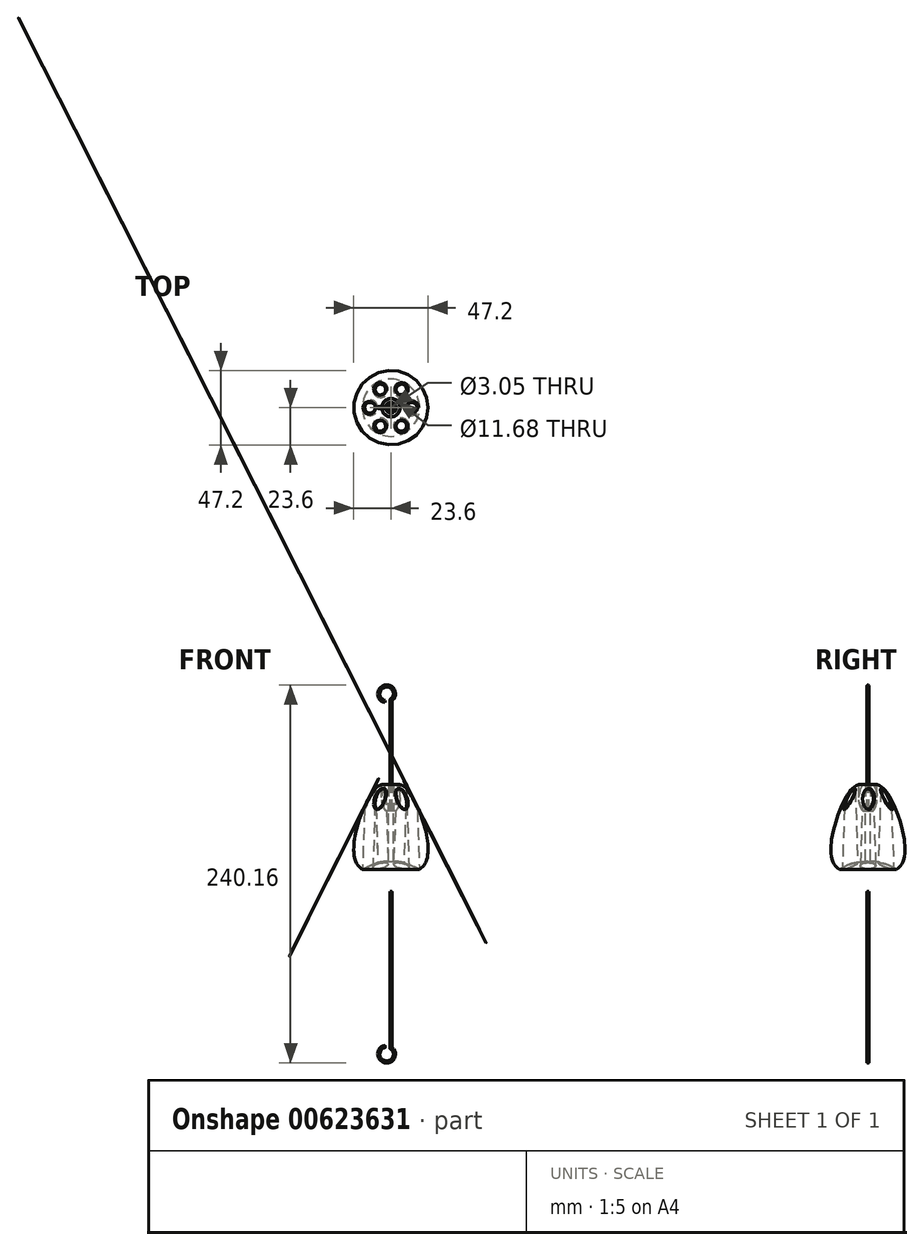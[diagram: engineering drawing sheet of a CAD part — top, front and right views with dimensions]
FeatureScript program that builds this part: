
annotation { "Feature Type Name" : "Feature", "Feature Type Description" : "" }
export const myFeature = defineFeature(function(context is Context, id is Id, definition is map)
    precondition{}
    {
        {
            var Q0;
            Q0=qCreatedBy(makeId("Front.planeOp"),FACE);
            var sketch = newSketch(context, id + "F0", { "sketchPlane" : qUnion([Q0])});
            skLineSegment(sketch, "E0", {"start": v(0, 64.62) * mm, "end": v(0, -10.1) * mm, "construction": true});
            skLineSegment(sketch, "E1", {"start": v(-12.7, 50.8) * mm, "end": v(12.7, 50.8) * mm, "construction": true});
            skLineSegment(sketch, "E2", {"start": v(-22.22, 7.62) * mm, "end": v(22.23, 7.62) * mm, "construction": true});
            skFitSpline(sketch, "E3", {"points": [v(0, 0) * mm, v(-22.23, 7.62) * mm, v(-12.7, 50.8) * mm, v(0, 57.15) * mm], "startDerivative": vector(-86.95, 0.17) * mm, "endDerivative": vector(69.55, -6.02) * mm});
            skLineSegment(sketch, "E4", {"start": v(-5.84, 48.51) * mm, "end": v(5.84, 48.51) * mm, "construction": true});
            skLineSegment(sketch, "E5", {"start": v(-3.3, 39.88) * mm, "end": v(0, 39.88) * mm});
            skArc(sketch, "E6", {"start": v(-5.84, 48.51) * mm, "mid": v(-5.2, 44.01) * mm, "end": v(-3.3, 39.88) * mm});
            skLineSegment(sketch, "E7", {"start": v(-5.84, 48.51) * mm, "end": v(-5.84, 56.75) * mm});
            skPoint(sketch, "E8.orphan", {"position": v(-3.3, 57.15) * mm});
            skPoint(sketch, "E9.orphan", {"position": v(3.3, 39.88) * mm});
            skPoint(sketch, "E10.end.orphan", {"position": v(3.3, 57.15) * mm});
            skLineSegment(sketch, "E11", {"start": v(0, 39.88) * mm, "end": v(0, 0) * mm});
            skSolve(sketch);
        }
        {
            var Q0;
            Q0 = qSketchRegion(id + "F0", true);
            var Q1;
            Q1=sQuery(id+"F0.wireOp",EDGE,"E0");
            revolve(context, id + "F1", {"entities" : qUnion([Q0]), "axis" : qUnion([Q1]), "revolveType" : RevolveType.FULL});
        }
        {
            var Q0;
            Q0=makeQuery(id+"F1.opRevolve","SWEPT_FACE",FACE,{"disambiguationData":[OSD([sQuery(id+"F0.wireOp",EDGE,"E5")])]});
            var sketch = newSketch(context, id + "F2", { "sketchPlane" : qUnion([Q0])});
            skCircle(sketch, "E12", {"center": v(0, 0) * mm, "radius": 1.52 * mm});
            skSolve(sketch);
        }
        {
            var Q0;
            Q0=qCreatedBy(makeId("Front.planeOp"),FACE);
            var sketch = newSketch(context, id + "F3", { "sketchPlane" : qUnion([Q0])});
            skLineSegment(sketch, "E13", {"start": v(-0.65, 101.6) * mm, "end": v(-0.65, -101.6) * mm});
            skLineSegment(sketch, "E14", {"start": v(-0.65, 101.6) * mm, "end": v(0, 101.6) * mm});
            skLineSegment(sketch, "E15", {"start": v(0, 101.6) * mm, "end": v(0, -101.6) * mm});
            skLineSegment(sketch, "E16", {"start": v(0, -101.6) * mm, "end": v(-0.65, -101.6) * mm});
            skLineSegment(sketch, "E17", {"start": v(0, 0) * mm, "end": v(0, -504.12) * mm, "construction": true});
            skSolve(sketch);
        }
        {
            var Q0;
            Q0 = qSketchRegion(id + "F3", true);
            var Q1;
            Q1=sQuery(id+"F3.wireOp",EDGE,"E17");
            revolve(context, id + "F4", {"entities" : qUnion([Q0]), "axis" : qUnion([Q1]), "revolveType" : RevolveType.FULL, "surfaceOperationType" : NewSurfaceOperationType.NEW});
        }
        {
            var Q0;
            Q0 = qSketchRegion(id + "F2", true);
            extrude(context, id + "F5", {"entities" : qUnion([Q0]), "operationType" : NewBodyOperationType.REMOVE, "oppositeDirection" : true, "depth" : 51.05 * mm, "offsetDistance" : 25.4 * mm});
        }
        {
            var Q0;
            Q0=qCreatedBy(makeId("Front.planeOp"),FACE);
            var sketch = newSketch(context, id + "F6", { "sketchPlane" : qUnion([Q0])});
            skPoint(sketch, "E18.0", {"position": v(3.3, 57.15) * mm});
            skPoint(sketch, "E18.1", {"position": v(5.84, 48.51) * mm});
            skPoint(sketch, "E18.2", {"position": v(3.3, 39.88) * mm});
            skArc(sketch, "E19", {"start": v(3.3, 39.88) * mm, "mid": v(5.84, 48.51) * mm, "end": v(3.3, 57.15) * mm, "construction": true});
            skArc(sketch, "E20.0", {"start": v(3.15, 39.88) * mm, "mid": v(5.71, 48.28) * mm, "end": v(3.4, 56.75) * mm});
            skLineSegment(sketch, "E21", {"start": v(3.4, 56.75) * mm, "end": v(1.52, 56.75) * mm});
            skLineSegment(sketch, "E22", {"start": v(1.52, 56.75) * mm, "end": v(1.82, 39.88) * mm});
            skLineSegment(sketch, "E23", {"start": v(3.15, 39.88) * mm, "end": v(1.82, 39.88) * mm});
            skSolve(sketch);
        }
        {
            var Q0;
            Q0 = qSketchRegion(id + "F6", true);
            var Q1;
            Q1=sQuery(id+"F0.wireOp",EDGE,"E11");
            revolve(context, id + "F7", {"entities" : qUnion([Q0]), "axis" : qUnion([Q1]), "revolveType" : RevolveType.FULL});
        }
        {
            var Q0;
            Q0=qCreatedBy(makeId("Front.planeOp"),FACE);
            var sketch = newSketch(context, id + "F8", { "sketchPlane" : qUnion([Q0])});
            skArc(sketch, "E24", {"start": v(-0.13, 8) * mm, "mid": v(-12.76, 5.81) * mm, "end": v(-23.46, -1.23) * mm});
            skLineSegment(sketch, "E25", {"start": v(-0.13, 8) * mm, "end": v(-0.13, -2.34) * mm});
            skLineSegment(sketch, "E26", {"start": v(-0.13, -2.34) * mm, "end": v(-23.46, -1.23) * mm});
            skSolve(sketch);
        }
        {
            var Q0;
            Q0 = qSketchRegion(id + "F8", true);
            var Q1;
            Q1=sQuery(id+"F0.wireOp",EDGE,"E11");
            revolve(context, id + "F9", {"operationType" : NewBodyOperationType.REMOVE, "entities" : qUnion([Q0]), "axis" : qUnion([Q1]), "revolveType" : RevolveType.FULL, "oppositeDirection" : true});
        }
        {
            var Q0;
            Q0=qCreatedBy(makeId("Top.planeOp"),FACE);
            var sketch = newSketch(context, id + "F10", { "sketchPlane" : qUnion([Q0])});
            skCircle(sketch, "E27", {"center": v(13.1, 0) * mm, "radius": 5.08 * mm});
            skCircle(sketch, "E28.1.0", {"center": v(6.55, 11.35) * mm, "radius": 5.08 * mm});
            skCircle(sketch, "E28.2.0", {"center": v(-6.55, 11.35) * mm, "radius": 5.08 * mm});
            skCircle(sketch, "E28.3.0", {"center": v(-13.1, 0) * mm, "radius": 5.08 * mm});
            skCircle(sketch, "E28.4.0", {"center": v(-6.55, -11.35) * mm, "radius": 5.08 * mm});
            skCircle(sketch, "E28.5.0", {"center": v(6.55, -11.35) * mm, "radius": 5.08 * mm});
            skPoint(sketch, "E28.center", {"position": v(0, 0) * mm});
            skSolve(sketch);
        }
        {
            var Q0;
            Q0 = qSketchRegion(id + "F10", true);
            extrude(context, id + "F11", {"entities" : qUnion([Q0]), "operationType" : NewBodyOperationType.REMOVE, "depth" : 59.84 * mm, "offsetDistance" : 25.4 * mm, "hasDraft" : true, "draftAngle" : 2 * degree, "draftPullDirection" : true});
        }
        {
            var Q0;
            Q0=makeQuery(id+"F11.boolean.opBoolean","INTERSECT",EDGE,{"derivedFrom":[makeQuery(id+"F1.opRevolve","SWEPT_FACE",FACE,{"disambiguationData":[OSD([sQuery(id+"F0.wireOp",EDGE,"E3")])]}),makeQuery(id+"F11.opExtrude","SWEPT_FACE",FACE,{"disambiguationData":[OSD([sQuery(id+"F10.wireOp",EDGE,"E28.1.0")])]})]});
            var Q1;
            Q1=makeQuery(id+"F11.boolean.opBoolean","INTERSECT",EDGE,{"derivedFrom":[makeQuery(id+"F1.opRevolve","SWEPT_FACE",FACE,{"disambiguationData":[OSD([sQuery(id+"F0.wireOp",EDGE,"E3")])]}),makeQuery(id+"F11.opExtrude","SWEPT_FACE",FACE,{"disambiguationData":[OSD([sQuery(id+"F10.wireOp",EDGE,"E27")])]})]});
            var Q2;
            Q2=makeQuery(id+"F11.boolean.opBoolean","INTERSECT",EDGE,{"derivedFrom":[makeQuery(id+"F1.opRevolve","SWEPT_FACE",FACE,{"disambiguationData":[OSD([sQuery(id+"F0.wireOp",EDGE,"E3")])]}),makeQuery(id+"F11.opExtrude","SWEPT_FACE",FACE,{"disambiguationData":[OSD([sQuery(id+"F10.wireOp",EDGE,"E28.5.0")])]})]});
            var Q3;
            Q3=makeQuery(id+"F11.boolean.opBoolean","INTERSECT",EDGE,{"derivedFrom":[makeQuery(id+"F1.opRevolve","SWEPT_FACE",FACE,{"disambiguationData":[OSD([sQuery(id+"F0.wireOp",EDGE,"E3")])]}),makeQuery(id+"F11.opExtrude","SWEPT_FACE",FACE,{"disambiguationData":[OSD([sQuery(id+"F10.wireOp",EDGE,"E28.4.0")])]})]});
            var Q4;
            Q4=makeQuery(id+"F11.boolean.opBoolean","INTERSECT",EDGE,{"derivedFrom":[makeQuery(id+"F1.opRevolve","SWEPT_FACE",FACE,{"disambiguationData":[OSD([sQuery(id+"F0.wireOp",EDGE,"E3")])]}),makeQuery(id+"F11.opExtrude","SWEPT_FACE",FACE,{"disambiguationData":[OSD([sQuery(id+"F10.wireOp",EDGE,"E28.3.0")])]})]});
            var Q5;
            Q5=makeQuery(id+"F11.boolean.opBoolean","INTERSECT",EDGE,{"derivedFrom":[makeQuery(id+"F1.opRevolve","SWEPT_FACE",FACE,{"disambiguationData":[OSD([sQuery(id+"F0.wireOp",EDGE,"E3")])]}),makeQuery(id+"F11.opExtrude","SWEPT_FACE",FACE,{"disambiguationData":[OSD([sQuery(id+"F10.wireOp",EDGE,"E28.2.0")])]})]});
            fillet(context, id + "F12", {"entities" : qUnion([Q0, Q1, Q2, Q3, Q4, Q5]), "radius" : 0.5 * mm, "tangentPropagation" : true, "allowEdgeOverflow" : false});
        }
        {
            var Q0;
            Q0=qCreatedBy(makeId("Front.planeOp"),FACE);
            var sketch = newSketch(context, id + "F13", { "sketchPlane" : qUnion([Q0])});
            skLineSegment(sketch, "E29", {"start": v(0, 101.6) * mm, "end": v(0, 110.07) * mm});
            skArc(sketch, "E30", {"start": v(1.38, 111.6) * mm, "mid": v(-4.6, 119.07) * mm, "end": v(-3.76, 109.54) * mm});
            skLineSegment(sketch, "E31", {"start": v(0.63, 111.17) * mm, "end": v(1.38, 111.6) * mm});
            skPoint(sketch, "E32.visualSharp", {"position": v(0, 110.8) * mm});
            skArc(sketch, "E32.filletArc", {"start": v(0.63, 111.17) * mm, "mid": v(0.17, 110.7) * mm, "end": v(0, 110.07) * mm});
            skLineSegment(sketch, "E33.0", {"start": v(-0.65, 101.6) * mm, "end": v(0.65, 101.6) * mm, "construction": true});
            skSolve(sketch);
        }
        {
            var Q0;
            Q0=makeQuery(id+"F4.opRevolve","SWEPT_FACE",FACE,{"disambiguationData":[OSD([sQuery(id+"F3.wireOp",EDGE,"E14")])]});
            var sketch = newSketch(context, id + "F14", { "sketchPlane" : qUnion([Q0])});
            skCircle(sketch, "E34.0", {"center": v(0, 0) * mm, "radius": 0.65 * mm});
            skSolve(sketch);
        }
        {
            var Q0;
            Q0=makeQuery(id+"F14.imprint","IMPRINT",FACE,{"disambiguationData":[TD([[makeQuery(id+"F14.imprint","IMPRINT",EDGE,{"derivedFrom":sQuery(id+"F14.wireOp",EDGE,"E34.0")}),1.0]])]});
            var Q1;
            Q1 = qConstructionFilter(qBodyType(qCreatedBy(id + "F13" ,EDGE), BodyType.WIRE), ConstructionObject.NO);
            sweep(context, id + "F15", {"profiles" : qUnion([Q0]), "path" : qUnion([Q1])});
        }
        {
            var Q0;
            Q0=makeQuery(id+"F15.opSweep","SWEPT_BODY",BODY,{"disambiguationData":[OSD([sQuery(id+"F13.wireOp",EDGE,"E29"),sQuery(id+"F14.wireOp",EDGE,"E34.0")])]});
            var Q1;
            Q1=qCreatedBy(makeId("Top.planeOp"),FACE);
            mirror(context, id + "F16", {"operationType" : NewBodyOperationType.ADD, "entities" : qUnion([Q0]), "mirrorPlane" : qUnion([Q1])});
        }
    });
